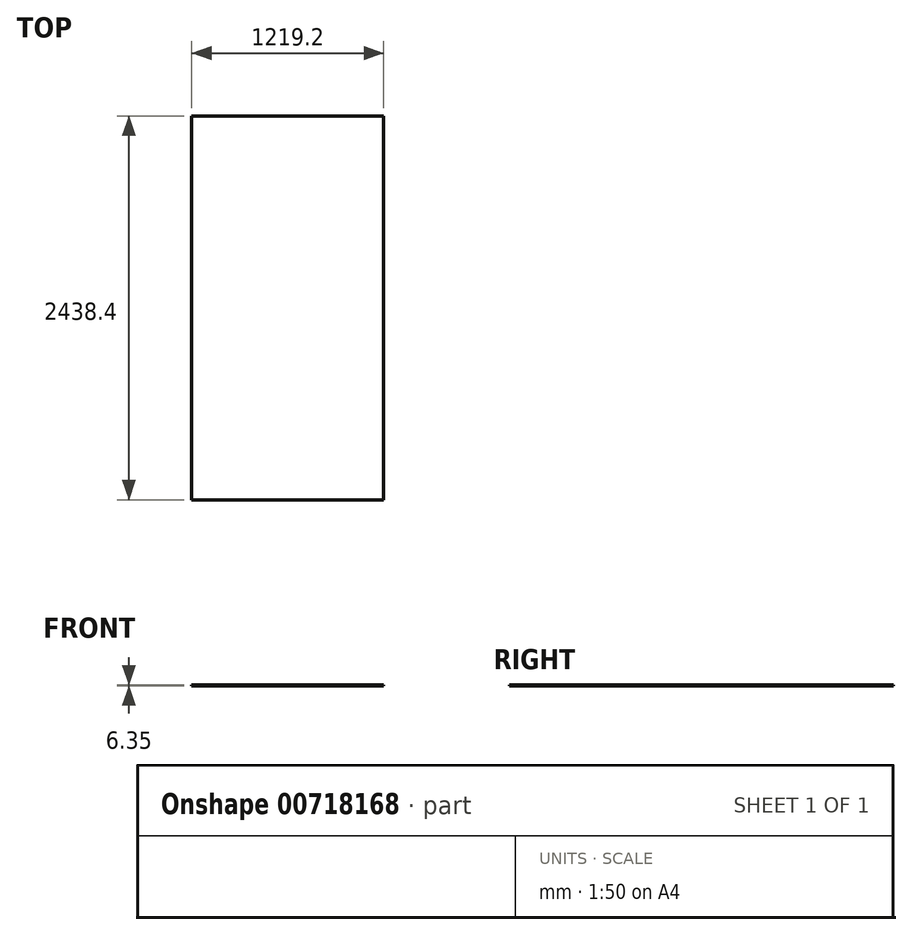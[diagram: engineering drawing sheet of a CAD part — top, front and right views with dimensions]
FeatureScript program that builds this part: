
annotation { "Feature Type Name" : "Feature", "Feature Type Description" : "" }
export const myFeature = defineFeature(function(context is Context, id is Id, definition is map)
    precondition{}
    {
        {
            var Q0;
            Q0=qCreatedBy(makeId("Top.planeOp"),FACE);
            var sketch = newSketch(context, id + "F0", { "sketchPlane" : qUnion([Q0])});
            skLineSegment(sketch, "E0.bottom", {"start": v(-609.6, 1219.2) * mm, "end": v(609.6, 1219.2) * mm});
            skLineSegment(sketch, "E0.top", {"start": v(-609.6, -1219.2) * mm, "end": v(609.6, -1219.2) * mm});
            skLineSegment(sketch, "E0.left", {"start": v(-609.6, 1219.2) * mm, "end": v(-609.6, -1219.2) * mm});
            skLineSegment(sketch, "E0.right", {"start": v(609.6, 1219.2) * mm, "end": v(609.6, -1219.2) * mm});
            skPoint(sketch, "E0.middle", {"position": v(0, 0) * mm});
            skSolve(sketch);
        }
        {
            var Q0;
            Q0 = qSketchRegion(id + "F0", true);
            extrude(context, id + "F1", {"entities" : qUnion([Q0]), "depth" : 6.35 * mm, "offsetDistance" : 25.4 * mm});
        }
    });
